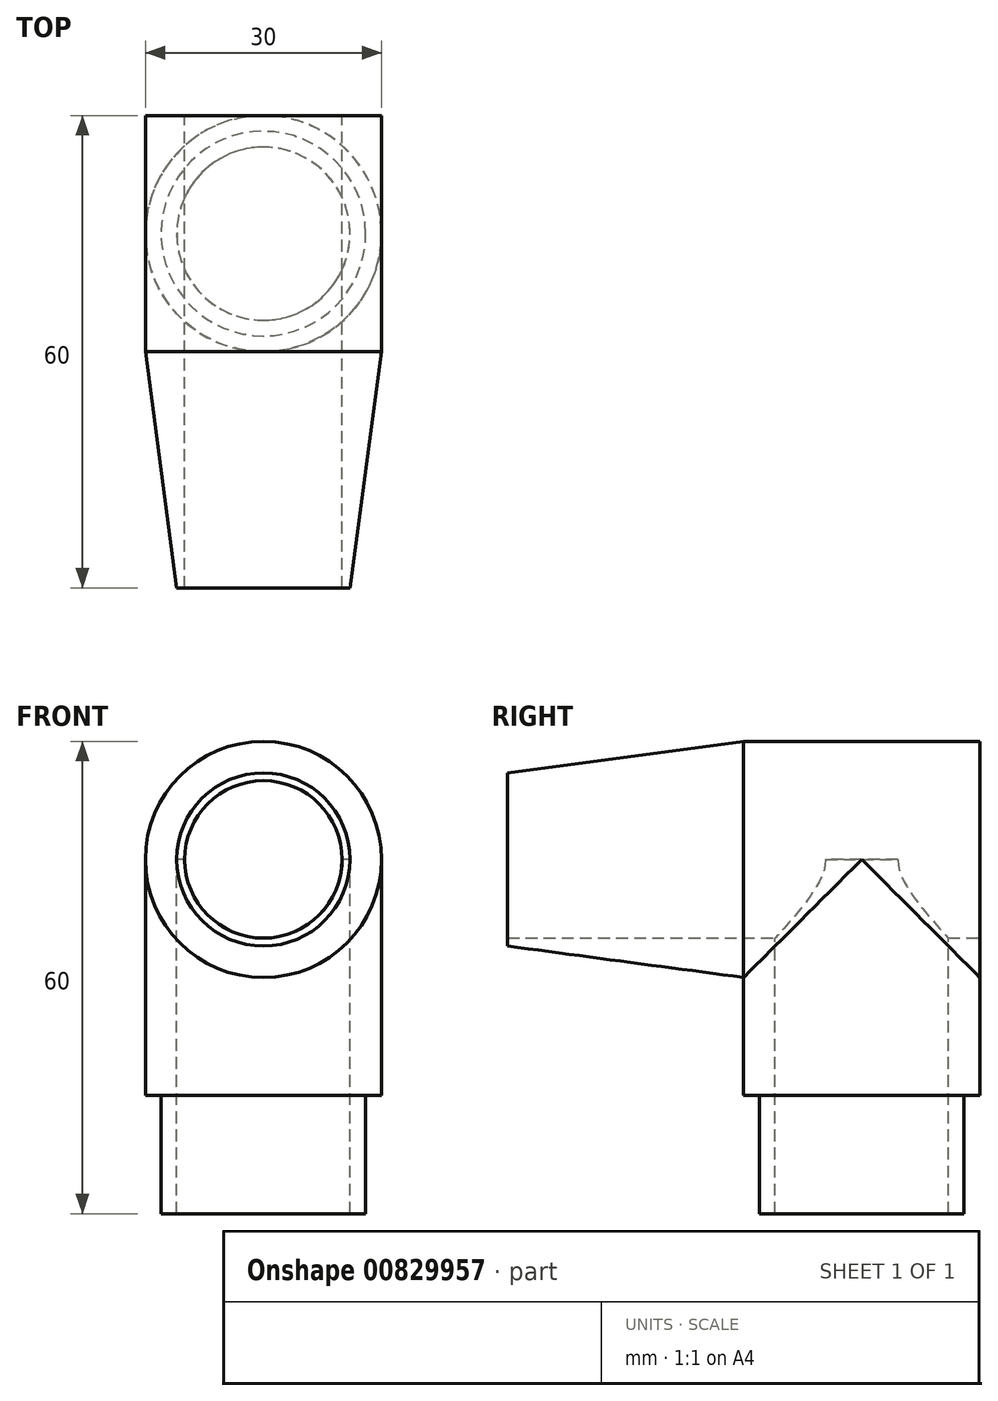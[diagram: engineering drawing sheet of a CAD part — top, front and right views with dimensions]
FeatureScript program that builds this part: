
annotation { "Feature Type Name" : "Feature", "Feature Type Description" : "" }
export const myFeature = defineFeature(function(context is Context, id is Id, definition is map)
    precondition{}
    {
        {
            var Q0;
            Q0=qCreatedBy(makeId("Front.planeOp"),FACE);
            var sketch = newSketch(context, id + "F0", { "sketchPlane" : qUnion([Q0])});
            skCircle(sketch, "E0", {"center": v(0, 0) * mm, "radius": 10 * mm});
            skCircle(sketch, "E1", {"center": v(0, 0) * mm, "radius": 15 * mm});
            skSolve(sketch);
        }
        {
            var Q0;
            Q0=makeQuery(id+"F0.imprint","IMPRINT",FACE,{"disambiguationData":[TD([[makeQuery(id+"F0.imprint","IMPRINT",EDGE,{"derivedFrom":sQuery(id+"F0.wireOp",EDGE,"E0")}),-1.0]])]});
            extrude(context, id + "F1", {"entities" : qUnion([Q0]), "depth" : 15 * mm, "offsetDistance" : 25 * mm, "hasSecondDirection" : true, "secondDirectionOppositeDirection" : true, "secondDirectionDepth" : 15 * mm});
        }
        {
            var Q0;
            Q0=qCreatedBy(makeId("Top.planeOp"),FACE);
            var sketch = newSketch(context, id + "F2", { "sketchPlane" : qUnion([Q0])});
            skCircle(sketch, "E2", {"center": v(0, 0) * mm, "radius": 11 * mm});
            skCircle(sketch, "E3", {"center": v(0, 0) * mm, "radius": 15 * mm});
            skSolve(sketch);
        }
        {
            var Q0;
            Q0 = qSketchRegion(id + "F2", true);
            extrude(context, id + "F3", {"entities" : qUnion([Q0]), "operationType" : NewBodyOperationType.ADD, "oppositeDirection" : true, "depth" : 30 * mm, "offsetDistance" : 25 * mm});
        }
        {
            var Q0;
            Q0=makeQuery(id+"F0.imprint","IMPRINT",FACE,{"disambiguationData":[TD([[makeQuery(id+"F0.imprint","IMPRINT",EDGE,{"derivedFrom":sQuery(id+"F0.wireOp",EDGE,"E0")}),1.0]])]});
            var Q1;
            Q1=sQuery(id+"F0.wireOp",EDGE,"E0");
            var Q2;
            Q2=makeQuery(id+"F1.opExtrude","CAP_FACE",FACE,{"disambiguationData":[OSD([sQuery(id+"F0.wireOp",EDGE,"E0"),sQuery(id+"F0.wireOp",EDGE,"E1")])],"isStart":false});
            var Q3;
            Q3=makeQuery(id+"F1.opExtrude","CAP_FACE",FACE,{"disambiguationData":[OSD([sQuery(id+"F0.wireOp",EDGE,"E0"),sQuery(id+"F0.wireOp",EDGE,"E1")])],"isStart":true});
            extrude(context, id + "F4", {"entities" : qUnion([Q0]), "operationType" : NewBodyOperationType.REMOVE, "surfaceEntities" : qUnion([Q1]), "endBound" : BoundingType.UP_TO_SURFACE, "depth" : 25 * mm, "endBoundEntityFace" : qUnion([Q2]), "offsetDistance" : 25 * mm, "hasSecondDirection" : true, "secondDirectionBound" : BoundingType.UP_TO_SURFACE, "secondDirectionOppositeDirection" : true, "secondDirectionDepth" : 25 * mm, "secondDirectionBoundEntityFace" : qUnion([Q3])});
        }
        {
            var Q0;
            Q0=makeQuery(id+"F2.imprint","IMPRINT",FACE,{"disambiguationData":[TD([[makeQuery(id+"F2.imprint","IMPRINT",EDGE,{"derivedFrom":sQuery(id+"F2.wireOp",EDGE,"E2")}),1.0]])]});
            var Q1;
            Q1=sQuery(id+"F2.wireOp",EDGE,"E2");
            var Q2;
            Q2=makeQuery(id+"F3.opExtrude","CAP_FACE",FACE,{"disambiguationData":[OSD([sQuery(id+"F2.wireOp",EDGE,"E2"),sQuery(id+"F2.wireOp",EDGE,"E3")])],"isStart":false});
            extrude(context, id + "F5", {"entities" : qUnion([Q0]), "operationType" : NewBodyOperationType.REMOVE, "surfaceEntities" : qUnion([Q1]), "endBound" : BoundingType.UP_TO_SURFACE, "oppositeDirection" : true, "depth" : 25 * mm, "endBoundEntityFace" : qUnion([Q2]), "offsetDistance" : 25 * mm});
        }
        {
            var Q0;
            Q0=makeQuery(id+"F3.opExtrude","CAP_FACE",FACE,{"disambiguationData":[OSD([sQuery(id+"F2.wireOp",EDGE,"E2"),sQuery(id+"F2.wireOp",EDGE,"E3")])],"isStart":false});
            var sketch = newSketch(context, id + "F6", { "sketchPlane" : qUnion([Q0])});
            skCircle(sketch, "E4.0", {"center": v(0, 0) * mm, "radius": 11 * mm});
            skCircle(sketch, "E5", {"center": v(0, 0) * mm, "radius": 13 * mm});
            skSolve(sketch);
        }
        {
            var Q0;
            Q0 = qSketchRegion(id + "F6", true);
            extrude(context, id + "F7", {"entities" : qUnion([Q0]), "operationType" : NewBodyOperationType.ADD, "depth" : 15 * mm, "offsetDistance" : 25 * mm});
        }
        {
            var Q0;
            Q0=qCreatedBy(makeId("Right.planeOp"),FACE);
            var sketch = newSketch(context, id + "F8", { "sketchPlane" : qUnion([Q0])});
            skLineSegment(sketch, "E6", {"start": v(-15, 15) * mm, "end": v(-45, 11) * mm});
            skLineSegment(sketch, "E7", {"start": v(-45, 11) * mm, "end": v(-45, 10) * mm});
            skLineSegment(sketch, "E8", {"start": v(-64.97, 0) * mm, "end": v(26.82, 0) * mm, "construction": true});
            skLineSegment(sketch, "E9", {"start": v(-45, 10) * mm, "end": v(-15, 10) * mm});
            skLineSegment(sketch, "E10", {"start": v(-15, 10) * mm, "end": v(-15, 15) * mm});
            skLineSegment(sketch, "E11", {"start": v(-15, 15) * mm, "end": v(15, 15) * mm, "construction": true});
            skLineSegment(sketch, "E12.0.0", {"start": v(-15, -15) * mm, "end": v(0, 0) * mm});
            skLineSegment(sketch, "E12.0.1", {"start": v(0, 0) * mm, "end": v(15, -15) * mm});
            skLineSegment(sketch, "E12.0.2", {"start": v(15, -15) * mm, "end": v(15, 15) * mm});
            skLineSegment(sketch, "E12.0.3", {"start": v(15, -15) * mm, "end": v(0, 0) * mm});
            skLineSegment(sketch, "E12.0.4", {"start": v(0, 0) * mm, "end": v(-15, -15) * mm});
            skLineSegment(sketch, "E12.0.5", {"start": v(-15, 15) * mm, "end": v(-15, -15) * mm});
            skLineSegment(sketch, "E13", {"start": v(-11, -10) * mm, "end": v(-15, -10) * mm});
            skLineSegment(sketch, "E14", {"start": v(-15, 10) * mm, "end": v(15, 10) * mm, "construction": true});
            skLineSegment(sketch, "E15", {"start": v(15, -10) * mm, "end": v(11, -10) * mm});
            skSolve(sketch);
        }
        {
            var Q0;
            {var subQ0=sQuery(id+"F8.wireOp",EDGE,"E6");Q0=makeQuery(id+"F8.imprint","IMPRINT",FACE,{"disambiguationData":[TD([[makeQuery(id+"F8.imprint","IMPRINT",EDGE,{"derivedFrom":subQ0}),1.0]])]});}
            var Q1;
            Q1=sQuery(id+"F8.wireOp",EDGE,"E8");
            revolve(context, id + "F9", {"operationType" : NewBodyOperationType.ADD, "surfaceOperationType" : NewSurfaceOperationType.NEW, "entities" : qUnion([Q0]), "axis" : qUnion([Q1]), "revolveType" : RevolveType.FULL});
        }
    });
